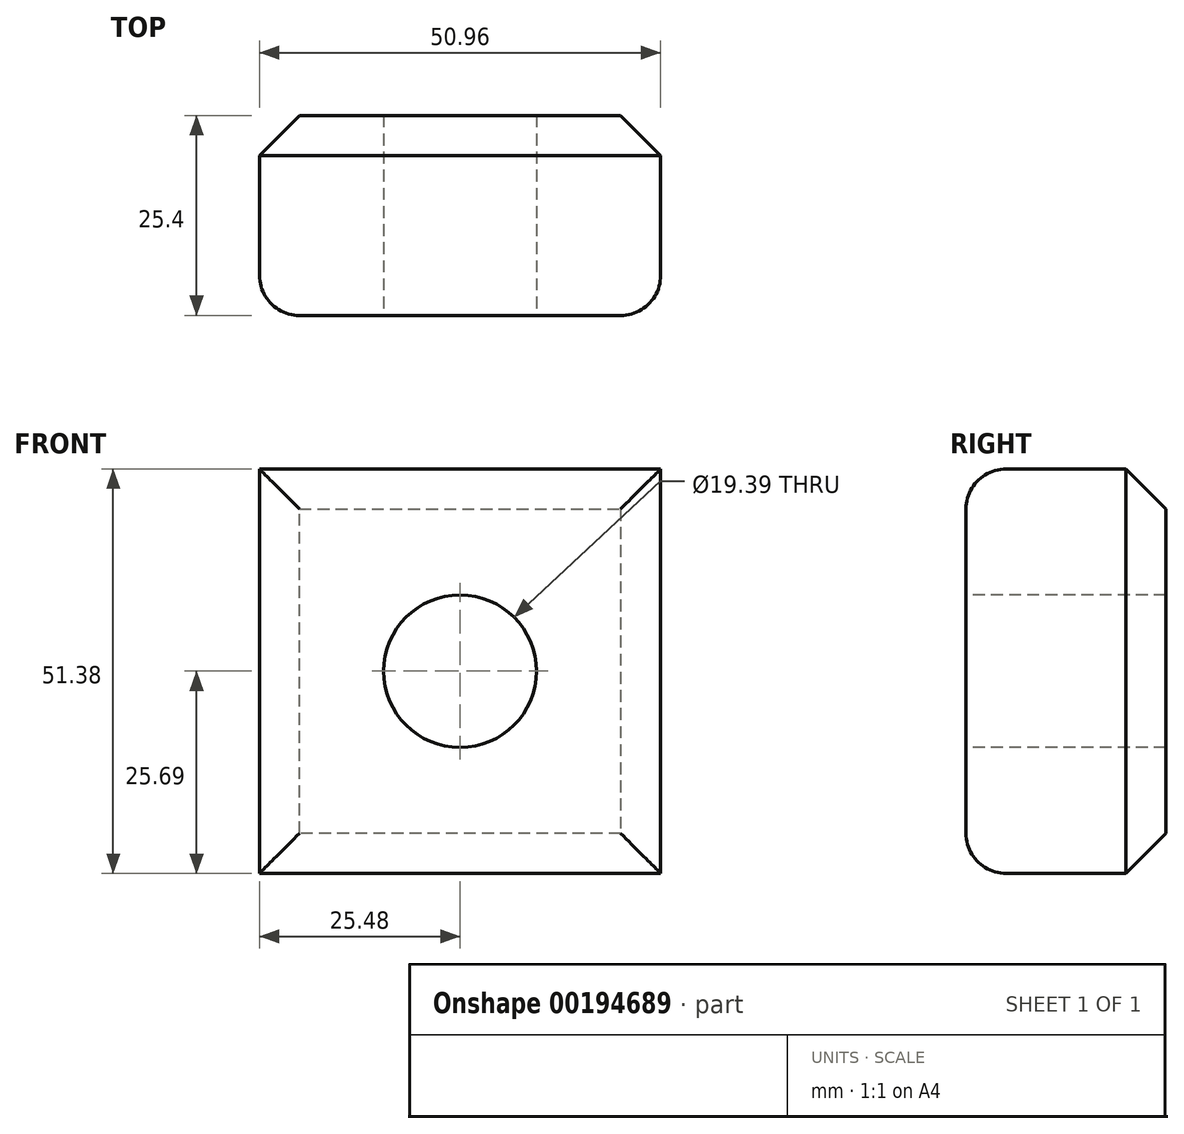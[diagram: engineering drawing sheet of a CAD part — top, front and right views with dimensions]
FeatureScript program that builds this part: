
annotation { "Feature Type Name" : "Feature", "Feature Type Description" : "" }
export const myFeature = defineFeature(function(context is Context, id is Id, definition is map)
    precondition{}
    {
        {
            var Q0;
            Q0=qCreatedBy(makeId("Front.planeOp"),FACE);
            var sketch = newSketch(context, id + "F0", { "sketchPlane" : qUnion([Q0])});
            skLineSegment(sketch, "E0.bottom", {"start": v(25.48, 25.69) * mm, "end": v(-25.48, 25.69) * mm});
            skLineSegment(sketch, "E0.top", {"start": v(25.48, -25.69) * mm, "end": v(-25.48, -25.69) * mm});
            skLineSegment(sketch, "E0.left", {"start": v(25.48, 25.69) * mm, "end": v(25.48, -25.69) * mm});
            skLineSegment(sketch, "E0.right", {"start": v(-25.48, 25.69) * mm, "end": v(-25.48, -25.69) * mm});
            skPoint(sketch, "E0.middle", {"position": v(0, 0) * mm});
            skSolve(sketch);
        }
        {
            var Q0;
            Q0=makeQuery(id+"F0.imprint","IMPRINT",FACE,{"disambiguationData":[TD([[makeQuery(id+"F0.imprint","IMPRINT",EDGE,{"derivedFrom":sQuery(id+"F0.wireOp",EDGE,"E0.bottom")}),1.0]])]});
            extrude(context, id + "F1", {"entities" : qUnion([Q0]), "depth" : 25.4 * mm});
        }
        {
            var Q0;
            Q0=makeQuery(id+"F1.opExtrude","CAP_EDGE",EDGE,{"disambiguationData":[OSD([sQuery(id+"F0.wireOp",EDGE,"E0.bottom")])],"isStart":false});
            var Q1;
            Q1=makeQuery(id+"F1.opExtrude","CAP_EDGE",EDGE,{"disambiguationData":[OSD([sQuery(id+"F0.wireOp",EDGE,"E0.left")])],"isStart":false});
            var Q2;
            Q2=makeQuery(id+"F1.opExtrude","CAP_EDGE",EDGE,{"disambiguationData":[OSD([sQuery(id+"F0.wireOp",EDGE,"E0.top")])],"isStart":false});
            var Q3;
            Q3=makeQuery(id+"F1.opExtrude","CAP_FACE",FACE,{"disambiguationData":[OSD([sQuery(id+"F0.wireOp",EDGE,"E0.bottom"),sQuery(id+"F0.wireOp",EDGE,"E0.top"),sQuery(id+"F0.wireOp",EDGE,"E0.left"),sQuery(id+"F0.wireOp",EDGE,"E0.right")])],"isStart":false});
            fillet(context, id + "F2", {"entities" : qUnion([Q0, Q1, Q2, Q3]), "radius" : 5.08 * mm, "tangentPropagation" : true, "allowEdgeOverflow" : false});
        }
        {
            var Q0;
            Q0=makeQuery(id+"F1.opExtrude","CAP_EDGE",EDGE,{"disambiguationData":[OSD([sQuery(id+"F0.wireOp",EDGE,"E0.bottom")])],"isStart":true});
            var Q1;
            Q1=makeQuery(id+"F1.opExtrude","CAP_EDGE",EDGE,{"disambiguationData":[OSD([sQuery(id+"F0.wireOp",EDGE,"E0.right")])],"isStart":true});
            var Q2;
            Q2=makeQuery(id+"F1.opExtrude","CAP_EDGE",EDGE,{"disambiguationData":[OSD([sQuery(id+"F0.wireOp",EDGE,"E0.top")])],"isStart":true});
            var Q3;
            Q3=makeQuery(id+"F1.opExtrude","CAP_EDGE",EDGE,{"disambiguationData":[OSD([sQuery(id+"F0.wireOp",EDGE,"E0.left")])],"isStart":true});
            chamfer(context, id + "F3", {"entities" : qUnion([Q0, Q1, Q2, Q3]), "width" : 5.08 * mm, "tangentPropagation" : true});
        }
        {
            var Q0;
            Q0=makeQuery(id+"F1.opExtrude","CAP_FACE",FACE,{"disambiguationData":[OSD([sQuery(id+"F0.wireOp",EDGE,"E0.bottom"),sQuery(id+"F0.wireOp",EDGE,"E0.top"),sQuery(id+"F0.wireOp",EDGE,"E0.left"),sQuery(id+"F0.wireOp",EDGE,"E0.right")])],"isStart":false});
            var sketch = newSketch(context, id + "F4", { "sketchPlane" : qUnion([Q0])});
            skCircle(sketch, "E1", {"center": v(0, 0) * mm, "radius": 9.7 * mm});
            skSolve(sketch);
        }
        {
            var Q0;
            Q0=makeQuery(id+"F4.imprint","IMPRINT",FACE,{"disambiguationData":[TD([[makeQuery(id+"F4.imprint","IMPRINT",EDGE,{"derivedFrom":sQuery(id+"F4.wireOp",EDGE,"E1")}),1.0]])]});
            extrude(context, id + "F5", {"entities" : qUnion([Q0]), "operationType" : NewBodyOperationType.REMOVE, "oppositeDirection" : true, "depth" : 25.4 * mm});
        }
    });
